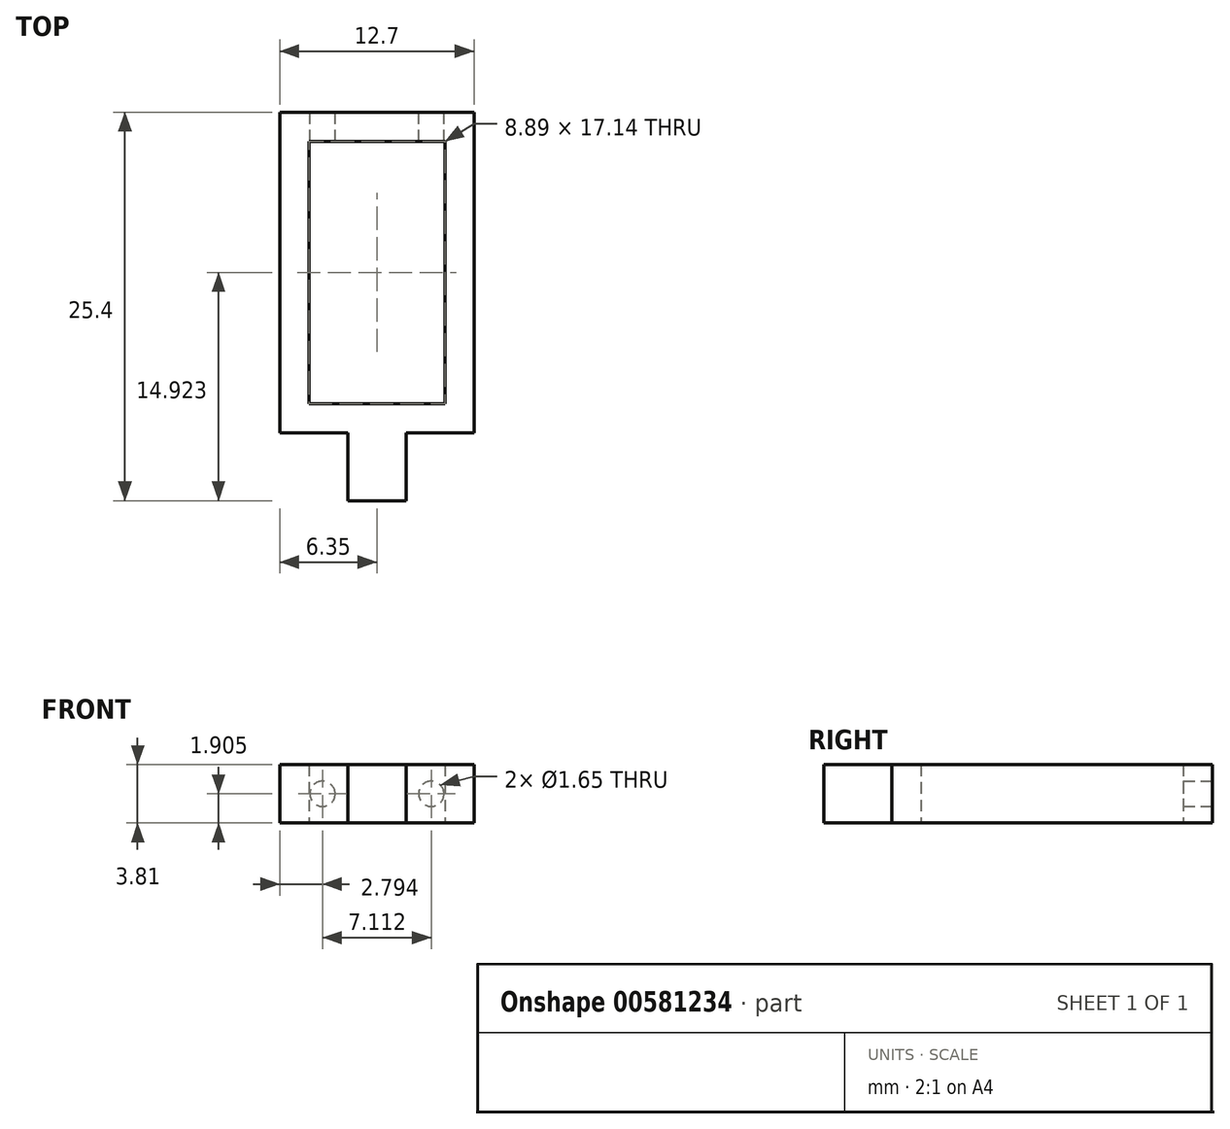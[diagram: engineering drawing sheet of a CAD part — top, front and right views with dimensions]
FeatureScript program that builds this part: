
annotation { "Feature Type Name" : "Feature", "Feature Type Description" : "" }
export const myFeature = defineFeature(function(context is Context, id is Id, definition is map)
    precondition{}
    {
        {
            var Q0;
            Q0=qCreatedBy(makeId("Top.planeOp"),FACE);
            var sketch = newSketch(context, id + "F0", { "sketchPlane" : qUnion([Q0])});
            skLineSegment(sketch, "E0.bottom", {"start": v(1.9, -13.97) * mm, "end": v(-1.9, -13.97) * mm});
            skLineSegment(sketch, "E0.top", {"start": v(6.35, 11.43) * mm, "end": v(-6.35, 11.43) * mm});
            skLineSegment(sketch, "E0.left", {"start": v(6.35, -9.52) * mm, "end": v(6.35, 11.43) * mm});
            skLineSegment(sketch, "E0.right", {"start": v(-6.35, -9.52) * mm, "end": v(-6.35, 11.43) * mm});
            skPoint(sketch, "E0.middle", {"position": v(0, 0) * mm});
            skLineSegment(sketch, "E1.top", {"start": v(-6.35, -9.53) * mm, "end": v(-1.9, -9.53) * mm});
            skLineSegment(sketch, "E1.right", {"start": v(-1.9, -13.97) * mm, "end": v(-1.9, -9.53) * mm});
            skLineSegment(sketch, "E2.top", {"start": v(6.35, -9.53) * mm, "end": v(1.9, -9.53) * mm});
            skLineSegment(sketch, "E2.right", {"start": v(1.9, -13.97) * mm, "end": v(1.9, -9.53) * mm});
            skLineSegment(sketch, "E3.bottom", {"start": v(-4.44, -7.62) * mm, "end": v(4.45, -7.62) * mm});
            skLineSegment(sketch, "E3.top", {"start": v(-4.45, 9.52) * mm, "end": v(4.44, 9.52) * mm});
            skLineSegment(sketch, "E3.left", {"start": v(-4.44, -7.62) * mm, "end": v(-4.45, 9.52) * mm});
            skLineSegment(sketch, "E3.right", {"start": v(4.45, -7.62) * mm, "end": v(4.44, 9.52) * mm});
            skSolve(sketch);
        }
        {
            var Q0;
            Q0=makeQuery(id+"F0.imprint","IMPRINT",FACE,{"disambiguationData":[TD([[makeQuery(id+"F0.imprint","IMPRINT",EDGE,{"derivedFrom":sQuery(id+"F0.wireOp",EDGE,"E0.bottom")}),-1.0]])]});
            extrude(context, id + "F1", {"entities" : qUnion([Q0]), "depth" : 3.8 * mm, "offsetDistance" : 25.4 * mm});
        }
        {
            var Q0;
            Q0=makeQuery(id+"F1.opExtrude","SWEPT_FACE",FACE,{"disambiguationData":[OSD([sQuery(id+"F0.wireOp",EDGE,"E0.top")])]});
            var sketch = newSketch(context, id + "F2", { "sketchPlane" : qUnion([Q0])});
            skCircle(sketch, "E4", {"center": v(-3.56, 1.9) * mm, "radius": 0.83 * mm});
            skCircle(sketch, "E5.MirrorC", {"center": v(3.56, 1.9) * mm, "radius": 0.83 * mm});
            skSolve(sketch);
        }
        {
            var Q0;
            Q0 = qSketchRegion(id + "F2", true);
            extrude(context, id + "F3", {"entities" : qUnion([Q0]), "operationType" : NewBodyOperationType.REMOVE, "oppositeDirection" : true, "depth" : 2.03 * mm, "offsetDistance" : 25.4 * mm});
        }
    });
